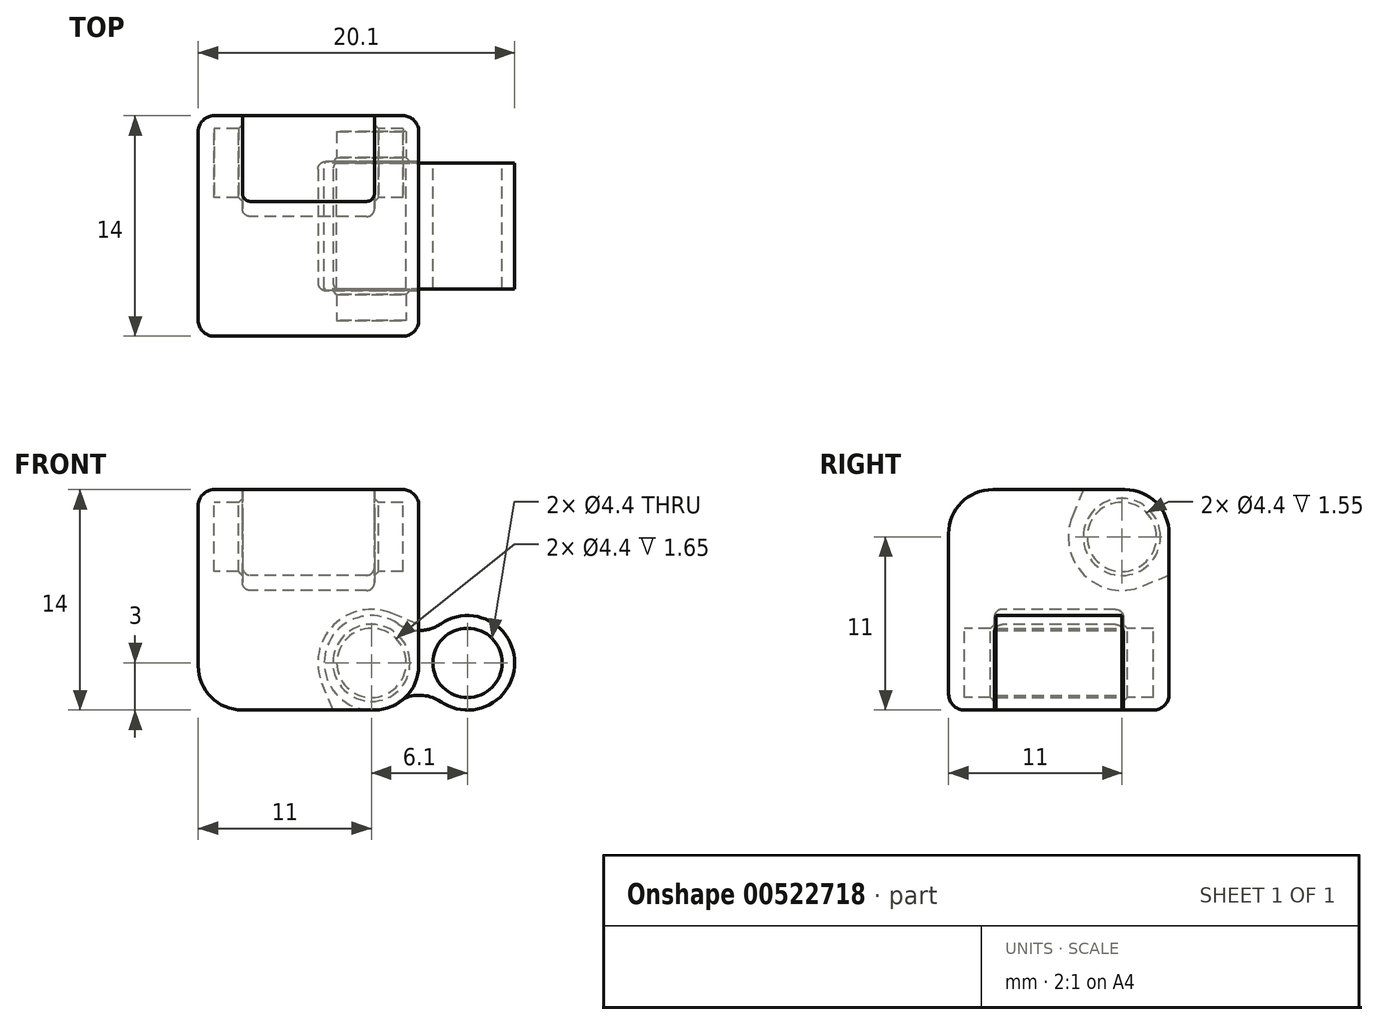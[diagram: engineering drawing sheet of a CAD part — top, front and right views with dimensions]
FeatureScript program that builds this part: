
annotation { "Feature Type Name" : "Feature", "Feature Type Description" : "" }
export const myFeature = defineFeature(function(context is Context, id is Id, definition is map)
    precondition{}
    {
        {
            assignVariable(context, id + "F0", {"name" : "magnetDiameter", "anyValue" : 4});
        }
        {
            assignVariable(context, id + "F1", {"name" : "magnetLength", "anyValue" : 4});
        }
        {
            assignVariable(context, id + "F2", {"name" : "extrusionWidth", "anyValue" : .4});
        }
        {
            assignVariable(context, id + "F3", {"name" : "cubeSize", "anyValue" : getVariable(context, 'magnetLength') * 3 + getVariable(context, 'extrusionWidth') * 5});
        }
        {
            var Q0;
            Q0=qCreatedBy(makeId("Top.planeOp"),FACE);
            var sketch = newSketch(context, id + "F4", { "sketchPlane" : qUnion([Q0])});
            skLineSegment(sketch, "E0.bottom", {"start": v(7, -7) * mm, "end": v(-7, -7) * mm});
            skLineSegment(sketch, "E0.top", {"start": v(7, 7) * mm, "end": v(-7, 7) * mm});
            skLineSegment(sketch, "E0.left", {"start": v(7, -7) * mm, "end": v(7, 7) * mm});
            skLineSegment(sketch, "E0.right", {"start": v(-7, -7) * mm, "end": v(-7, 7) * mm});
            skPoint(sketch, "E0.middle", {"position": v(0, 0) * mm});
            skSolve(sketch);
        }
        {
            var Q0;
            Q0 = qSketchRegion(id + "F4", true);
            extrude(context, id + "F5", {"entities" : qUnion([Q0]), "depth" : (getVariable(context, 'cubeSize')) * mm, "offsetDistance" : 25 * mm});
        }
        {
            var Q0;
            Q0=qCreatedBy(makeId("Front.planeOp"),FACE);
            var sketch = newSketch(context, id + "F6", { "sketchPlane" : qUnion([Q0])});
            skCircle(sketch, "E1", {"center": v(4, 3) * mm, "radius": 2.2 * mm});
            skLineSegment(sketch, "E2", {"start": v(4, 3) * mm, "end": v(6.2, 3) * mm, "construction": true});
            skLineSegment(sketch, "E3", {"start": v(6.2, 3) * mm, "end": v(7, 3) * mm, "construction": true});
            skLineSegment(sketch, "E4", {"start": v(4, 0) * mm, "end": v(4, 0.8) * mm, "construction": true});
            skLineSegment(sketch, "E5", {"start": v(4, 0.8) * mm, "end": v(4, 3) * mm, "construction": true});
            skLineSegment(sketch, "E6", {"start": v(7, 0) * mm, "end": v(1.56, 0) * mm});
            skLineSegment(sketch, "E7", {"start": v(1.56, 0) * mm, "end": v(0.86, 1.7) * mm});
            skLineSegment(sketch, "E8", {"start": v(7, 0) * mm, "end": v(7, 5.44) * mm});
            skLineSegment(sketch, "E9", {"start": v(7, 5.44) * mm, "end": v(5.3, 6.14) * mm});
            skArc(sketch, "E10", {"start": v(5.3, 6.14) * mm, "mid": v(1.6, 5.4) * mm, "end": v(0.86, 1.7) * mm});
            skSolve(sketch);
        }
        {
            assignVariable(context, id + "F7", {"name" : "hingeSize", "anyValue" : getVariable(context, 'magnetLength') * 2});
        }
        {
            var Q0;
            Q0=makeQuery(id+"F6.imprint","IMPRINT",FACE,{"disambiguationData":[TD([[makeQuery(id+"F6.imprint","IMPRINT",EDGE,{"derivedFrom":sQuery(id+"F6.wireOp",EDGE,"E1")}),-1.0]])]});
            var Q1;
            Q1=makeQuery(id+"F6.imprint","IMPRINT",FACE,{"disambiguationData":[TD([[makeQuery(id+"F6.imprint","IMPRINT",EDGE,{"derivedFrom":sQuery(id+"F6.wireOp",EDGE,"E1")}),1.0]])]});
            extrude(context, id + "F8", {"entities" : qUnion([Q0, Q1]), "operationType" : NewBodyOperationType.REMOVE, "endBound" : BoundingType.SYMMETRIC, "oppositeDirection" : true, "depth" : (getVariable(context, 'hingeSize') + 0.2) * mm, "offsetDistance" : 25 * mm});
        }
        {
            var Q0;
            Q0=makeQuery(id+"F6.imprint","IMPRINT",FACE,{"disambiguationData":[TD([[makeQuery(id+"F6.imprint","IMPRINT",EDGE,{"derivedFrom":sQuery(id+"F6.wireOp",EDGE,"E1")}),1.0]])]});
            extrude(context, id + "F9", {"entities" : qUnion([Q0]), "operationType" : NewBodyOperationType.REMOVE, "endBound" : BoundingType.SYMMETRIC, "oppositeDirection" : true, "depth" : (getVariable(context, 'hingeSize') + getVariable(context, 'magnetLength')) * mm, "offsetDistance" : 25 * mm});
        }
        {
            var Q0;
            Q0=qCreatedBy(makeId("Right.planeOp"),FACE);
            var sketch = newSketch(context, id + "F10", { "sketchPlane" : qUnion([Q0])});
            skCircle(sketch, "E11", {"center": v(4, 11) * mm, "radius": 2.2 * mm});
            skLineSegment(sketch, "E12", {"start": v(1.56, 14) * mm, "end": v(7, 14) * mm});
            skLineSegment(sketch, "E13", {"start": v(7, 14) * mm, "end": v(7, 8.56) * mm});
            skLineSegment(sketch, "E14", {"start": v(7, 8.56) * mm, "end": v(5.3, 7.86) * mm});
            skLineSegment(sketch, "E15", {"start": v(1.56, 14) * mm, "end": v(0.86, 12.3) * mm});
            skLineSegment(sketch, "E16", {"start": v(4, 11) * mm, "end": v(6.2, 11) * mm, "construction": true});
            skLineSegment(sketch, "E17", {"start": v(6.2, 11) * mm, "end": v(7, 11) * mm, "construction": true});
            skLineSegment(sketch, "E18", {"start": v(4, 11) * mm, "end": v(4, 13.2) * mm, "construction": true});
            skLineSegment(sketch, "E19", {"start": v(4, 13.2) * mm, "end": v(4, 14) * mm, "construction": true});
            skArc(sketch, "E20", {"start": v(0.86, 12.3) * mm, "mid": v(1.6, 8.6) * mm, "end": v(5.3, 7.86) * mm});
            skSolve(sketch);
        }
        {
            var Q0;
            Q0=makeQuery(id+"F10.imprint","IMPRINT",FACE,{"disambiguationData":[TD([[makeQuery(id+"F10.imprint","IMPRINT",EDGE,{"derivedFrom":sQuery(id+"F10.wireOp",EDGE,"E11")}),1.0]])]});
            var Q1;
            Q1=makeQuery(id+"F10.imprint","IMPRINT",FACE,{"disambiguationData":[TD([[makeQuery(id+"F10.imprint","IMPRINT",EDGE,{"derivedFrom":sQuery(id+"F10.wireOp",EDGE,"E11")}),-1.0]])]});
            extrude(context, id + "F11", {"entities" : qUnion([Q0, Q1]), "operationType" : NewBodyOperationType.REMOVE, "endBound" : BoundingType.SYMMETRIC, "depth" : (getVariable(context, 'hingeSize') + 0.4) * mm, "offsetDistance" : 25 * mm});
        }
        {
            var Q0;
            Q0=makeQuery(id+"F10.imprint","IMPRINT",FACE,{"disambiguationData":[TD([[makeQuery(id+"F10.imprint","IMPRINT",EDGE,{"derivedFrom":sQuery(id+"F10.wireOp",EDGE,"E11")}),1.0]])]});
            extrude(context, id + "F12", {"entities" : qUnion([Q0]), "operationType" : NewBodyOperationType.REMOVE, "endBound" : BoundingType.SYMMETRIC, "depth" : (getVariable(context, 'hingeSize') + getVariable(context, 'magnetLength')) * mm, "offsetDistance" : 25 * mm});
        }
        {
            var Q0;
            {var subQ0=sQuery(id+"F4.wireOp",EDGE,"E0.bottom");var subQ1=sQuery(id+"F4.wireOp",EDGE,"E0.left");Q0=makeQuery(id+"F8.boolean.opBoolean","SPLIT",EDGE,{"disambiguationData":[TD([makeQuery(id+"F5.opExtrude","SWEPT_FACE",FACE,{"disambiguationData":[OSD([subQ0])]})])],"derivedFrom":makeQuery(id+"F5.opExtrude","CAP_EDGE",EDGE,{"disambiguationData":[OSD([subQ1])],"isStart":true})});}
            var Q1;
            {var subQ0=sQuery(id+"F4.wireOp",EDGE,"E0.left");var subQ1=sQuery(id+"F4.wireOp",EDGE,"E0.top");Q1=makeQuery(id+"F8.boolean.opBoolean","SPLIT",EDGE,{"disambiguationData":[TD([makeQuery(id+"F5.opExtrude","SWEPT_FACE",FACE,{"disambiguationData":[OSD([subQ1])]})])],"derivedFrom":makeQuery(id+"F5.opExtrude","CAP_EDGE",EDGE,{"disambiguationData":[OSD([subQ0])],"isStart":true})});}
            var Q2;
            {var subQ0=sQuery(id+"F4.wireOp",EDGE,"E0.right");var subQ1=sQuery(id+"F4.wireOp",EDGE,"E0.top");Q2=makeQuery(id+"F11.boolean.opBoolean","SPLIT",EDGE,{"disambiguationData":[TD([makeQuery(id+"F5.opExtrude","SWEPT_FACE",FACE,{"disambiguationData":[OSD([subQ0])]})])],"derivedFrom":makeQuery(id+"F5.opExtrude","CAP_EDGE",EDGE,{"disambiguationData":[OSD([subQ1])],"isStart":false})});}
            var Q3;
            {var subQ0=sQuery(id+"F4.wireOp",EDGE,"E0.left");var subQ1=sQuery(id+"F4.wireOp",EDGE,"E0.top");Q3=makeQuery(id+"F11.boolean.opBoolean","SPLIT",EDGE,{"disambiguationData":[TD([makeQuery(id+"F5.opExtrude","SWEPT_FACE",FACE,{"disambiguationData":[OSD([subQ0])]})])],"derivedFrom":makeQuery(id+"F5.opExtrude","CAP_EDGE",EDGE,{"disambiguationData":[OSD([subQ1])],"isStart":false})});}
            var Q4;
            Q4=makeQuery(id+"F5.opExtrude","CAP_EDGE",EDGE,{"disambiguationData":[OSD([sQuery(id+"F4.wireOp",EDGE,"E0.bottom")])],"isStart":false});
            var Q5;
            Q5=makeQuery(id+"F5.opExtrude","CAP_EDGE",EDGE,{"disambiguationData":[OSD([sQuery(id+"F4.wireOp",EDGE,"E0.right")])],"isStart":true});
            fillet(context, id + "F13", {"entities" : qUnion([Q0, Q1, Q2, Q3, Q4, Q5]), "radius" : (getVariable(context, 'magnetDiameter') / 2 + getVariable(context, 'extrusionWidth') * 2) * mm, "tangentPropagation" : true, "allowEdgeOverflow" : false});
        }
        {
            var Q0;
            Q0=makeQuery(id+"F8.boolean.opBoolean","COPY",EDGE,{"derivedFrom":makeQuery(id+"F8.opExtrude","CAP_EDGE",EDGE,{"disambiguationData":[OSD([sQuery(id+"F6.wireOp",EDGE,"E7")])],"isStart":true})});
            var Q1;
            Q1=makeQuery(id+"F8.boolean.opBoolean","COPY",EDGE,{"derivedFrom":makeQuery(id+"F8.opExtrude","CAP_EDGE",EDGE,{"disambiguationData":[OSD([sQuery(id+"F6.wireOp",EDGE,"E7")])],"isStart":false})});
            var Q2;
            Q2=makeQuery(id+"F11.boolean.opBoolean","COPY",EDGE,{"derivedFrom":makeQuery(id+"F11.opExtrude","CAP_EDGE",EDGE,{"disambiguationData":[OSD([sQuery(id+"F10.wireOp",EDGE,"E14")])],"isStart":false})});
            var Q3;
            Q3=makeQuery(id+"F11.boolean.opBoolean","COPY",EDGE,{"derivedFrom":makeQuery(id+"F11.opExtrude","CAP_EDGE",EDGE,{"disambiguationData":[OSD([sQuery(id+"F10.wireOp",EDGE,"E14")])],"isStart":true})});
            fillet(context, id + "F14", {"entities" : qUnion([Q0, Q1, Q2, Q3]), "radius" : .5 * mm, "tangentPropagation" : true, "allowEdgeOverflow" : false});
        }
        {
            var Q0;
            Q0=qCreatedBy(makeId("Front.planeOp"),FACE);
            var sketch = newSketch(context, id + "F15", { "sketchPlane" : qUnion([Q0])});
            skCircle(sketch, "E21", {"center": v(4, 3) * mm, "radius": 2.2 * mm});
            skArc(sketch, "E22", {"start": v(5.7, 5.48) * mm, "mid": v(1, 3) * mm, "end": v(5.7, 0.52) * mm});
            skArc(sketch, "E23", {"start": v(8.4, 0.52) * mm, "mid": v(13.1, 3) * mm, "end": v(8.4, 5.48) * mm});
            skLineSegment(sketch, "E24", {"start": v(4, 3) * mm, "end": v(7, 3) * mm, "construction": true});
            skCircle(sketch, "E25", {"center": v(10.1, 3) * mm, "radius": 2.2 * mm});
            skLineSegment(sketch, "E26", {"start": v(7, 3) * mm, "end": v(7.1, 3) * mm, "construction": true});
            skLineSegment(sketch, "E27", {"start": v(7.1, 3) * mm, "end": v(10.1, 3) * mm, "construction": true});
            skArc(sketch, "E28", {"start": v(5.7, 5.48) * mm, "mid": v(7.05, 5.06) * mm, "end": v(8.4, 5.48) * mm});
            skArc(sketch, "E29", {"start": v(8.4, 0.52) * mm, "mid": v(7.05, 0.94) * mm, "end": v(5.7, 0.52) * mm});
            skLineSegment(sketch, "E30", {"start": v(7.05, -1.46) * mm, "end": v(7.05, 3) * mm, "construction": true});
            skLineSegment(sketch, "E31", {"start": v(7.05, 3) * mm, "end": v(7.05, 7.46) * mm, "construction": true});
            skSolve(sketch);
        }
        {
            var Q0;
            Q0=makeQuery(id+"F15.imprint","IMPRINT",FACE,{"disambiguationData":[TD([[makeQuery(id+"F15.imprint","IMPRINT",EDGE,{"derivedFrom":sQuery(id+"F15.wireOp",EDGE,"E21")}),-1.0]])]});
            extrude(context, id + "F16", {"entities" : qUnion([Q0]), "endBound" : BoundingType.SYMMETRIC, "depth" : (getVariable(context, 'hingeSize')) * mm, "offsetDistance" : 25 * mm});
        }
        {
            var Q0;
            Q0=makeQuery(id+"F9.boolean.opBoolean","INTERSECT",EDGE,{"derivedFrom":[makeQuery(id+"F8.boolean.opBoolean","COPY",FACE,{"derivedFrom":makeQuery(id+"F8.opExtrude","CAP_FACE",FACE,{"disambiguationData":[OSD([sQuery(id+"F6.wireOp",EDGE,"E6"),sQuery(id+"F6.wireOp",EDGE,"E7"),sQuery(id+"F6.wireOp",EDGE,"E8"),sQuery(id+"F6.wireOp",EDGE,"E9"),sQuery(id+"F6.wireOp",EDGE,"E10")])],"isStart":false})}),makeQuery(id+"F9.opExtrude","SWEPT_FACE",FACE,{"disambiguationData":[OSD([sQuery(id+"F6.wireOp",EDGE,"E1")])]})]});
            var Q1;
            Q1=makeQuery(id+"F9.boolean.opBoolean","INTERSECT",EDGE,{"derivedFrom":[makeQuery(id+"F8.boolean.opBoolean","COPY",FACE,{"derivedFrom":makeQuery(id+"F8.opExtrude","CAP_FACE",FACE,{"disambiguationData":[OSD([sQuery(id+"F6.wireOp",EDGE,"E6"),sQuery(id+"F6.wireOp",EDGE,"E7"),sQuery(id+"F6.wireOp",EDGE,"E8"),sQuery(id+"F6.wireOp",EDGE,"E9"),sQuery(id+"F6.wireOp",EDGE,"E10")])],"isStart":true})}),makeQuery(id+"F9.opExtrude","SWEPT_FACE",FACE,{"disambiguationData":[OSD([sQuery(id+"F6.wireOp",EDGE,"E1")])]})]});
            var Q2;
            Q2=makeQuery(id+"F12.boolean.opBoolean","INTERSECT",EDGE,{"derivedFrom":[makeQuery(id+"F11.boolean.opBoolean","COPY",FACE,{"derivedFrom":makeQuery(id+"F11.opExtrude","CAP_FACE",FACE,{"disambiguationData":[OSD([sQuery(id+"F10.wireOp",EDGE,"E12"),sQuery(id+"F10.wireOp",EDGE,"E13"),sQuery(id+"F10.wireOp",EDGE,"E14"),sQuery(id+"F10.wireOp",EDGE,"E15"),sQuery(id+"F10.wireOp",EDGE,"E20")])],"isStart":true})}),makeQuery(id+"F12.opExtrude","SWEPT_FACE",FACE,{"disambiguationData":[OSD([sQuery(id+"F10.wireOp",EDGE,"E11")])]})]});
            var Q3;
            Q3=makeQuery(id+"F12.boolean.opBoolean","INTERSECT",EDGE,{"derivedFrom":[makeQuery(id+"F11.boolean.opBoolean","COPY",FACE,{"derivedFrom":makeQuery(id+"F11.opExtrude","CAP_FACE",FACE,{"disambiguationData":[OSD([sQuery(id+"F10.wireOp",EDGE,"E12"),sQuery(id+"F10.wireOp",EDGE,"E13"),sQuery(id+"F10.wireOp",EDGE,"E14"),sQuery(id+"F10.wireOp",EDGE,"E15"),sQuery(id+"F10.wireOp",EDGE,"E20")])],"isStart":false})}),makeQuery(id+"F12.opExtrude","SWEPT_FACE",FACE,{"disambiguationData":[OSD([sQuery(id+"F10.wireOp",EDGE,"E11")])]})]});
            chamfer(context, id + "F17", {"entities" : qUnion([Q0, Q1, Q2, Q3]), "width" : .25 * mm, "tangentPropagation" : true});
        }
        {
            var Q0;
            Q0=makeQuery(id+"F5.opExtrude","CAP_EDGE",EDGE,{"disambiguationData":[OSD([sQuery(id+"F4.wireOp",EDGE,"E0.right")])],"isStart":false});
            fillet(context, id + "F18", {"entities" : qUnion([Q0]), "radius" : 1 * mm, "tangentPropagation" : true, "allowEdgeOverflow" : false});
        }
    });
